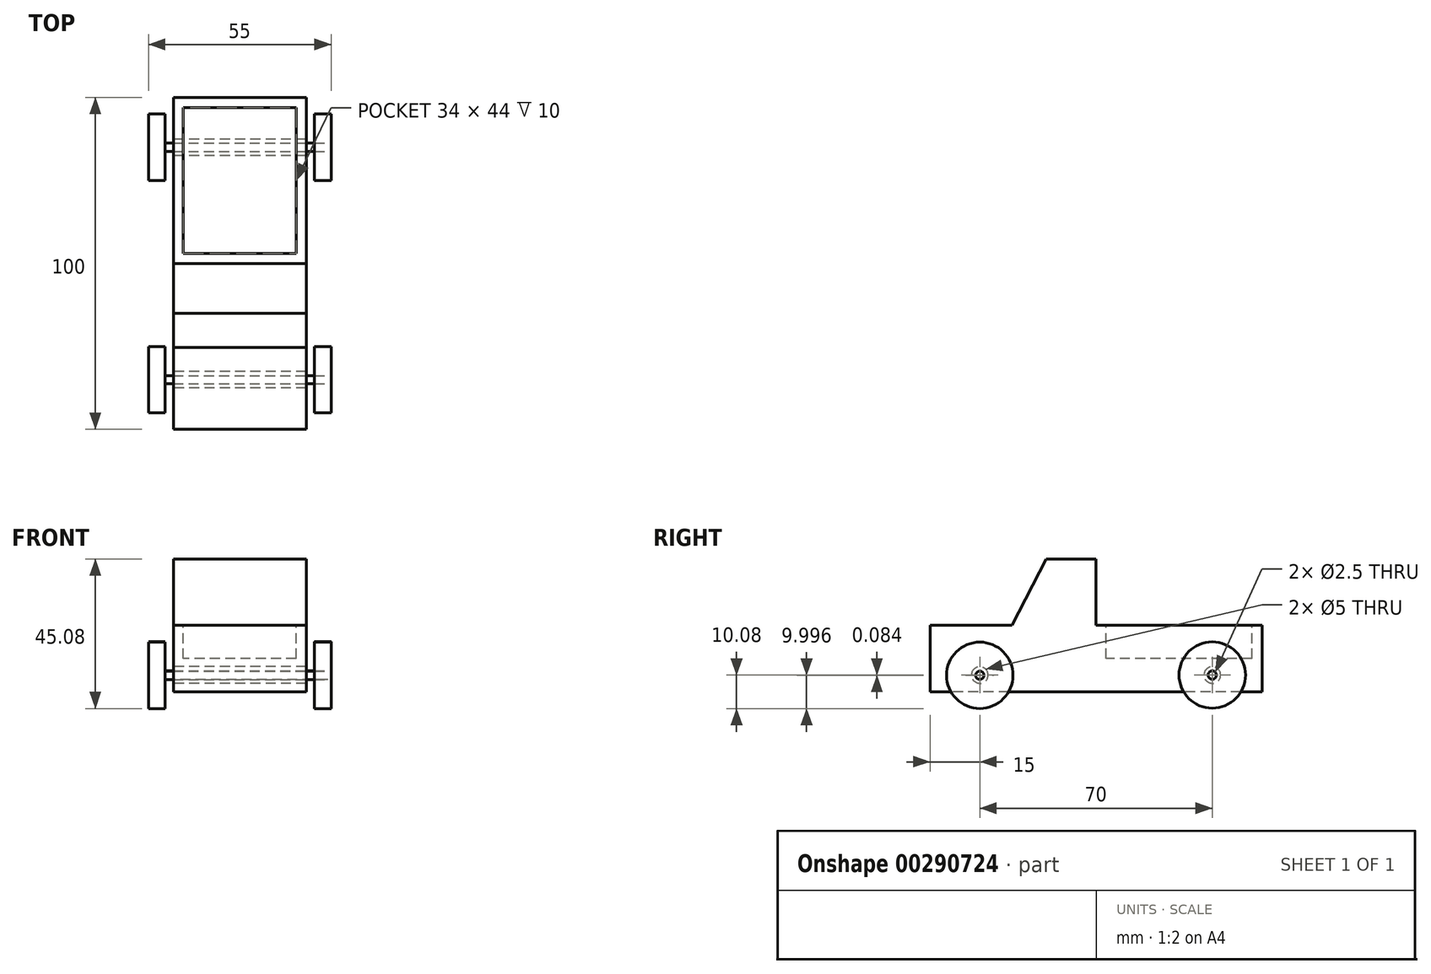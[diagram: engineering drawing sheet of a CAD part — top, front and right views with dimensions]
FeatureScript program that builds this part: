
annotation { "Feature Type Name" : "Feature", "Feature Type Description" : "" }
export const myFeature = defineFeature(function(context is Context, id is Id, definition is map)
    precondition{}
    {
        {
            var Q0;
            Q0=qCreatedBy(makeId("Right.planeOp"),FACE);
            var sketch = newSketch(context, id + "F0", { "sketchPlane" : qUnion([Q0])});
            skLineSegment(sketch, "E0.bottom", {"start": v(50, 10) * mm, "end": v(-50, 10) * mm});
            skLineSegment(sketch, "E0.top", {"start": v(50, -10) * mm, "end": v(-50, -10) * mm});
            skLineSegment(sketch, "E0.left", {"start": v(50, 10) * mm, "end": v(50, -10) * mm});
            skLineSegment(sketch, "E0.right", {"start": v(-50, 10) * mm, "end": v(-50, -10) * mm});
            skPoint(sketch, "E0.middle", {"position": v(0, 0) * mm});
            skLineSegment(sketch, "E1", {"start": v(0, 10) * mm, "end": v(0, 30) * mm});
            skPoint(sketch, "E1.endSnap0", {"position": v(0, 10) * mm});
            skLineSegment(sketch, "E2", {"start": v(0, 30) * mm, "end": v(-15, 30) * mm});
            skLineSegment(sketch, "E3", {"start": v(-15, 30) * mm, "end": v(-25.3, 10) * mm});
            skCircle(sketch, "E4", {"center": v(-35, -5) * mm, "radius": 2.5 * mm});
            skCircle(sketch, "E5", {"center": v(35, -5) * mm, "radius": 2.5 * mm});
            skSolve(sketch);
        }
        {
            var Q0;
            Q0 = qSketchRegion(id + "F0", true);
            extrude(context, id + "F1", {"entities" : qUnion([Q0]), "depth" : 40 * mm});
        }
        {
            var Q0;
            {var subQ0=sQuery(id+"F0.wireOp",EDGE,"E0.bottom");Q0=makeQuery(id+"F1.opExtrude","SWEPT_FACE",FACE,{"disambiguationData":[OSD([subQ0]),TDD([makeQuery(id+"F0.imprint","IMPRINT",EDGE,{"disambiguationData":[TD([[makeQuery(id+"F0.imprint","INTERSECT",VERTEX,{"derivedFrom":[subQ0,sQuery(id+"F0.wireOp",EDGE,"E0.left")]}),-1.0]])],"derivedFrom":subQ0})])]});}
            var sketch = newSketch(context, id + "F2", { "sketchPlane" : qUnion([Q0])});
            skLineSegment(sketch, "E6.0", {"start": v(3, 47) * mm, "end": v(3, 3) * mm});
            skLineSegment(sketch, "E6.1", {"start": v(37, 47) * mm, "end": v(3, 47) * mm});
            skLineSegment(sketch, "E6.2", {"start": v(37, 3) * mm, "end": v(37, 47) * mm});
            skLineSegment(sketch, "E6.3", {"start": v(3, 3) * mm, "end": v(37, 3) * mm});
            skSolve(sketch);
        }
        {
            var Q0;
            Q0 = qSketchRegion(id + "F2", true);
            extrude(context, id + "F3", {"entities" : qUnion([Q0]), "operationType" : NewBodyOperationType.REMOVE, "oppositeDirection" : true, "depth" : 10 * mm});
        }
        {
            var Q0;
            Q0=makeQuery(id+"F1.opExtrude","CAP_FACE",FACE,{"disambiguationData":[OSD([sQuery(id+"F0.wireOp",EDGE,"E0.bottom"),sQuery(id+"F0.wireOp",EDGE,"E0.top"),sQuery(id+"F0.wireOp",EDGE,"E0.left"),sQuery(id+"F0.wireOp",EDGE,"E0.right"),sQuery(id+"F0.wireOp",EDGE,"E1"),sQuery(id+"F0.wireOp",EDGE,"E2"),sQuery(id+"F0.wireOp",EDGE,"E3"),sQuery(id+"F0.wireOp",EDGE,"E4"),sQuery(id+"F0.wireOp",EDGE,"E5")])],"isStart":false});
            var sketch = newSketch(context, id + "F4", { "sketchPlane" : qUnion([Q0])});
            skCircle(sketch, "E7", {"center": v(-35, -5.08) * mm, "radius": 1.25 * mm});
            skSolve(sketch);
        }
        {
            var Q0;
            Q0=makeQuery(id+"F4.imprint","IMPRINT",FACE,{"disambiguationData":[TD([[makeQuery(id+"F4.imprint","IMPRINT",EDGE,{"derivedFrom":sQuery(id+"F4.wireOp",EDGE,"E7")}),1.0]])]});
            extrude(context, id + "F5", {"entities" : qUnion([Q0]), "oppositeDirection" : true, "depth" : 47.5 * mm});
        }
        {
            var Q0;
            Q0=makeQuery(id+"F5.opExtrude","CAP_FACE",FACE,{"disambiguationData":[OSD([sQuery(id+"F4.wireOp",EDGE,"E7")])],"isStart":true});
            extrude(context, id + "F6", {"entities" : qUnion([Q0]), "operationType" : NewBodyOperationType.ADD, "depth" : 7.5 * mm});
        }
        {
            var Q0;
            Q0=makeQuery(id+"F1.opExtrude","CAP_FACE",FACE,{"disambiguationData":[OSD([sQuery(id+"F0.wireOp",EDGE,"E0.bottom"),sQuery(id+"F0.wireOp",EDGE,"E0.top"),sQuery(id+"F0.wireOp",EDGE,"E0.left"),sQuery(id+"F0.wireOp",EDGE,"E0.right"),sQuery(id+"F0.wireOp",EDGE,"E1"),sQuery(id+"F0.wireOp",EDGE,"E2"),sQuery(id+"F0.wireOp",EDGE,"E3"),sQuery(id+"F0.wireOp",EDGE,"E4"),sQuery(id+"F0.wireOp",EDGE,"E5")])],"isStart":false});
            var sketch = newSketch(context, id + "F7", { "sketchPlane" : qUnion([Q0])});
            skCircle(sketch, "E8", {"center": v(35, -5) * mm, "radius": 1.25 * mm});
            skSolve(sketch);
        }
        {
            var Q0;
            Q0=makeQuery(id+"F7.imprint","IMPRINT",FACE,{"disambiguationData":[TD([[makeQuery(id+"F7.imprint","IMPRINT",EDGE,{"derivedFrom":sQuery(id+"F7.wireOp",EDGE,"E8")}),1.0]])]});
            extrude(context, id + "F8", {"entities" : qUnion([Q0]), "oppositeDirection" : true, "depth" : 47.5 * mm});
        }
        {
            var Q0;
            Q0=makeQuery(id+"F8.opExtrude","CAP_FACE",FACE,{"disambiguationData":[OSD([sQuery(id+"F7.wireOp",EDGE,"E8")])],"isStart":true});
            extrude(context, id + "F9", {"entities" : qUnion([Q0]), "operationType" : NewBodyOperationType.ADD, "depth" : 7.5 * mm});
        }
        {
            var Q0;
            Q0=makeQuery(id+"F6.opExtrude","CAP_FACE",FACE,{"disambiguationData":[OSD([sQuery(id+"F4.wireOp",EDGE,"E7")])],"isStart":false});
            var sketch = newSketch(context, id + "F10", { "sketchPlane" : qUnion([Q0])});
            skCircle(sketch, "E9", {"center": v(-35, -5.08) * mm, "radius": 10 * mm});
            skSolve(sketch);
        }
        {
            var Q0;
            Q0=makeQuery(id+"F10.imprint","IMPRINT",FACE,{"disambiguationData":[TD([[makeQuery(id+"F10.imprint","IMPRINT",EDGE,{"derivedFrom":sQuery(id+"F10.wireOp",EDGE,"E9")}),1.0]])]});
            extrude(context, id + "F11", {"entities" : qUnion([Q0]), "oppositeDirection" : true, "depth" : 5 * mm});
        }
        {
            var Q0;
            Q0=makeQuery(id+"F9.opExtrude","CAP_FACE",FACE,{"disambiguationData":[OSD([sQuery(id+"F7.wireOp",EDGE,"E8")])],"isStart":false});
            var sketch = newSketch(context, id + "F12", { "sketchPlane" : qUnion([Q0])});
            skCircle(sketch, "E10", {"center": v(35, -5) * mm, "radius": 10 * mm});
            skSolve(sketch);
        }
        {
            var Q0;
            Q0=makeQuery(id+"F12.imprint","IMPRINT",FACE,{"disambiguationData":[TD([[makeQuery(id+"F12.imprint","IMPRINT",EDGE,{"derivedFrom":sQuery(id+"F12.wireOp",EDGE,"E10")}),1.0]])]});
            var sketch = newSketch(context, id + "F13", { "sketchPlane" : qUnion([Q0])});
            skSolve(sketch);
        }
        {
            var Q0;
            Q0 = qSketchRegion(id + "F13", true);
            var Q1;
            Q1=makeQuery(id+"F12.imprint","IMPRINT",FACE,{"disambiguationData":[TD([[makeQuery(id+"F12.imprint","IMPRINT",EDGE,{"derivedFrom":sQuery(id+"F12.wireOp",EDGE,"E10")}),1.0]])]});
            extrude(context, id + "F14", {"entities" : qUnion([Q0, Q1]), "oppositeDirection" : true, "depth" : 5 * mm});
        }
        {
            var Q0;
            Q0=makeQuery(id+"F5.opExtrude","CAP_FACE",FACE,{"disambiguationData":[OSD([sQuery(id+"F4.wireOp",EDGE,"E7")])],"isStart":false});
            var sketch = newSketch(context, id + "F15", { "sketchPlane" : qUnion([Q0])});
            skCircle(sketch, "E11", {"center": v(35, -5.08) * mm, "radius": 10 * mm});
            skSolve(sketch);
        }
        {
            var Q0;
            Q0=makeQuery(id+"F15.imprint","IMPRINT",FACE,{"disambiguationData":[TD([[makeQuery(id+"F15.imprint","IMPRINT",EDGE,{"derivedFrom":sQuery(id+"F15.wireOp",EDGE,"E11")}),1.0]])]});
            extrude(context, id + "F16", {"entities" : qUnion([Q0]), "operationType" : NewBodyOperationType.ADD, "oppositeDirection" : true, "depth" : 5 * mm});
        }
        {
            var Q0;
            Q0=makeQuery(id+"F8.opExtrude","CAP_FACE",FACE,{"disambiguationData":[OSD([sQuery(id+"F7.wireOp",EDGE,"E8")])],"isStart":false});
            var sketch = newSketch(context, id + "F17", { "sketchPlane" : qUnion([Q0])});
            skCircle(sketch, "E12", {"center": v(-35, -5) * mm, "radius": 10 * mm});
            skSolve(sketch);
        }
        {
            var Q0;
            Q0=makeQuery(id+"F17.imprint","IMPRINT",FACE,{"disambiguationData":[TD([[makeQuery(id+"F17.imprint","IMPRINT",EDGE,{"derivedFrom":sQuery(id+"F17.wireOp",EDGE,"E12")}),1.0]])]});
            extrude(context, id + "F18", {"entities" : qUnion([Q0]), "operationType" : NewBodyOperationType.ADD, "oppositeDirection" : true, "depth" : 5 * mm});
        }
    });
